# Revit family: Crealco Skyline Heavy Duty Sash Side Hung A
name_source: partatom
category: Windows
revit_build: Autodesk Revit 2014 (Build: 20130308_1515(x64)
units: mm (PartAtom-declared; Revit-internal decimal feet)

## types (6) — shared parameters
Clearvue Insulated LowE SHGC Value = 0.85
Clearvue Insulated SHGC Value = 0.85
Corrected Mullion Configuration = 2 mm  [stored 0.00656168 ft]
Custom Window Width = 590 mm  [stored 1.9357 ft]
Description = Side Hung Type A Standard Sash Window
Frame Profile Thickness = 41 mm  [stored 0.134514 ft]
Heavy Duty Sash = Yes
Intruderprufe Insulated LowE SHGC Value = 0.705
Intruderprufe Insulated SHGC Value = 0.705
Limit Sash Height Max = 1500 mm  [stored 4.92126 ft]
Limit Sash Height Min = 300 mm  [stored 0.984252 ft]
Limit Sash Width Max = 700 mm  [stored 2.29659 ft]
Limit Sash Width Min = 300 mm  [stored 0.984252 ft]
Limit Window Height Max = 1588 mm
Limit Window Height Min = 388 mm
Limit Window Width Min = 388 mm
Manufacturer = Crealco
Max System DG Unit Thickness = 25 mm  [stored 0.082021 ft]
Model = Skyline
Rough Width = 3 mm  [stored 0.00984252 ft]
Sash Side Gap = 44 mm
Standard Mullion Different = No
Standard Sash = No
URL = www.crealco.co.za
Wall Closure = By host
zero-valued in all types: Custom Frame Offset From Exterior

## per-type parameters (varying)
| type | Clearvue Insulated LowE U Value | Clearvue Insulated U Value | Clearvue SHGC Value | Clearvue U Value | Custom Windload | Custom Window Height | Energy Advantage SHGC Value | Energy Advantage U Value | Intruderprufe Insulated LowE U Value | Intruderprufe Insulated U Value | Intruderprufe LowE SHGC Value | Intruderprufe LowE U Value | Intruderprufe SHGC Value | Intruderprufe U Value | Toughened Safety SHGC Value | Toughened Safety U Value |
| 0600 x 0900mm 1000Pa | 3.96 | 3.96 | 0.456 | 6.17 | 1000 mm  [stored 3.28084 ft] | 890 mm  [stored 2.91995 ft] | 0.412 | 5.31 | 2.44 | 2.44 | 0.384 | 5.21 | 0.431 | 6.12 | 0.456 | 6.17 |
| 0600 x 0900mm 1500Pa | 3.96 | 3.96 | 0.456 | 6.17 | 1500 mm  [stored 4.92126 ft] | 890 mm  [stored 2.91995 ft] | 0.412 | 5.31 | 2.44 | 2.44 | 0.384 | 5.21 | 0.431 | 6.12 | 0.456 | 6.17 |
| 0600 x 0900mm 2000Pa | 3.96 | 3.96 | 0.456 | 6.17 | 2000 mm  [stored 6.56168 ft] | 890 mm  [stored 2.91995 ft] | 0.412 | 5.31 | 2.44 | 2.44 | 0.384 | 5.21 | 0.431 | 6.12 | 0.456 | 6.17 |
| 0600 x 1200mm 1000Pa | 4.12 | 4.12 | 0.486 | 6.15 | 1000 mm  [stored 3.28084 ft] | 1190 mm  [stored 3.9042 ft] | 0.439 | 5.19 | 2.54 | 2.54 | 0.409 | 5.09 | 0.459 | 6.09 | 0.486 | 6.15 |
| 0600 x 1200mm 1500Pa | 4.12 | 4.12 | 0.486 | 6.15 | 1500 mm  [stored 4.92126 ft] | 1190 mm  [stored 3.9042 ft] | 0.439 | 5.19 | 2.54 | 2.54 | 0.409 | 5.09 | 0.459 | 6.09 | 0.486 | 6.15 |
| 0600 x 1200mm 2000Pa | 4.12 | 4.12 | 0.486 | 6.15 | 2000 mm  [stored 6.56168 ft] | 1190 mm  [stored 3.9042 ft] | 0.439 | 5.19 | 2.54 | 2.54 | 0.409 | 5.09 | 0.459 | 6.09 | 0.486 | 6.15 |

note: [stored X ft] marks values corroborated as IEEE doubles in the binary element streams (Revit-internal decimal feet)

## geometry (parser evidence)
native form markers: Sweep x9
no freeform markers — native parametric forms only
